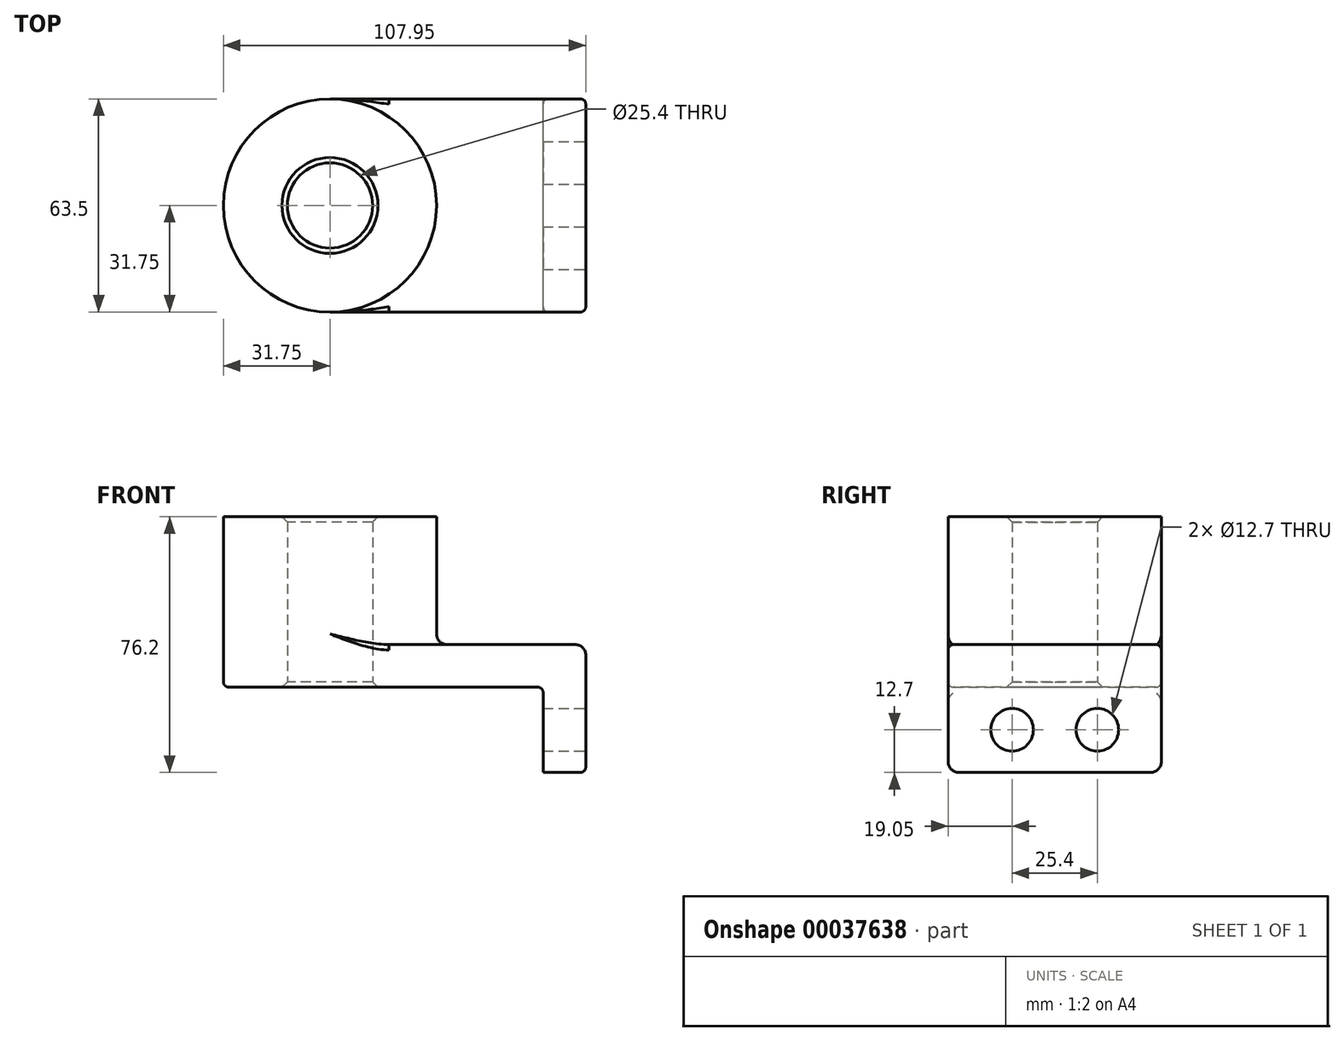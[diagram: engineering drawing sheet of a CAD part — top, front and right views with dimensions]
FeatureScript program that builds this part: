
annotation { "Feature Type Name" : "Feature", "Feature Type Description" : "" }
export const myFeature = defineFeature(function(context is Context, id is Id, definition is map)
    precondition{}
    {
        {
            var Q0;
            Q0=qCreatedBy(makeId("Top.planeOp"),FACE);
            var sketch = newSketch(context, id + "F0", { "sketchPlane" : qUnion([Q0])});
            skLineSegment(sketch, "E0.rect.bottom", {"start": v(38.1, -31.75) * mm, "end": v(-38.1, -31.75) * mm});
            skLineSegment(sketch, "E0.rect.top", {"start": v(38.1, 31.75) * mm, "end": v(-38.1, 31.75) * mm});
            skLineSegment(sketch, "E0.rect.left", {"start": v(38.1, -31.75) * mm, "end": v(38.1, 31.75) * mm});
            skLineSegment(sketch, "E0.rect.right", {"start": v(-38.1, -31.75) * mm, "end": v(-38.1, 31.75) * mm});
            skPoint(sketch, "E0.rect.middle", {"position": v(0, 0) * mm});
            skCircle(sketch, "E1", {"center": v(-38.1, 0) * mm, "radius": 31.75 * mm});
            skCircle(sketch, "E2", {"center": v(-38.1, 0) * mm, "radius": 12.7 * mm});
            skSolve(sketch);
        }
        {
            var Q0;
            Q0 = qSketchRegion(id + "F0", true);
            extrude(context, id + "F1", {"entities" : qUnion([Q0]), "depth" : 12.7 * mm});
        }
        {
            var Q0;
            {var subQ0=sQuery(id+"F0.wireOp",EDGE,"E2");var subQ1=sQuery(id+"F0.wireOp",EDGE,"E0.rect.right");var subQ3=makeQuery(id+"F0.imprint","INTERSECT",VERTEX,{"disambiguationData":[OD(0.0)],"derivedFrom":[subQ1,subQ0]});Q0=makeQuery(id+"F0.imprint","IMPRINT",FACE,{"disambiguationData":[TD([[makeQuery(id+"F0.imprint","IMPRINT",EDGE,{"disambiguationData":[TD([[subQ3,-1.0]])],"derivedFrom":subQ0}),-1.0]])]});}
            var Q1;
            {var subQ0=sQuery(id+"F0.wireOp",EDGE,"E2");var subQ1=sQuery(id+"F0.wireOp",EDGE,"E0.rect.right");var subQ3=makeQuery(id+"F0.imprint","INTERSECT",VERTEX,{"disambiguationData":[OD(0.0)],"derivedFrom":[subQ1,subQ0]});Q1=makeQuery(id+"F0.imprint","IMPRINT",FACE,{"disambiguationData":[TD([[makeQuery(id+"F0.imprint","IMPRINT",EDGE,{"disambiguationData":[TD([[subQ3,1.0]])],"derivedFrom":subQ0}),-1.0]])]});}
            var Q2;
            Q2=sQuery(id+"F0.wireOp",EDGE,"E1");
            var Q3;
            Q3=sQuery(id+"F0.wireOp",EDGE,"E2");
            extrude(context, id + "F2", {"entities" : qUnion([Q0, Q1]), "operationType" : NewBodyOperationType.ADD, "surfaceEntities" : qUnion([Q2, Q3]), "depth" : 50.8 * mm});
        }
        {
            var Q0;
            Q0=makeQuery(id+"F1.opExtrude","SWEPT_FACE",FACE,{"disambiguationData":[OSD([sQuery(id+"F0.wireOp",EDGE,"E0.rect.left")])]});
            var sketch = newSketch(context, id + "F3", { "sketchPlane" : qUnion([Q0])});
            skLineSegment(sketch, "E3.bottom", {"start": v(-31.75, 12.7) * mm, "end": v(31.75, 12.7) * mm});
            skLineSegment(sketch, "E3.top", {"start": v(-31.75, -25.4) * mm, "end": v(31.75, -25.4) * mm});
            skLineSegment(sketch, "E3.left", {"start": v(-31.75, 12.7) * mm, "end": v(-31.75, -25.4) * mm});
            skLineSegment(sketch, "E3.right", {"start": v(31.75, 12.7) * mm, "end": v(31.75, -25.4) * mm});
            skCircle(sketch, "E4", {"center": v(-12.7, -12.7) * mm, "radius": 6.35 * mm});
            skLineSegment(sketch, "E5", {"start": v(0, 0) * mm, "end": v(0, -25.4) * mm, "construction": true});
            skCircle(sketch, "E6.MirrorC", {"center": v(12.7, -12.7) * mm, "radius": 6.35 * mm});
            skSolve(sketch);
        }
        {
            var Q0;
            Q0 = qSketchRegion(id + "F3", true);
            extrude(context, id + "F4", {"entities" : qUnion([Q0]), "operationType" : NewBodyOperationType.ADD, "oppositeDirection" : true, "depth" : 12.7 * mm});
        }
        {
            var Q0;
            {var subQ0=sQuery(id+"F0.wireOp",EDGE,"E1");Q0=makeQuery(id+"F2.boolean.opBoolean","INTERSECT",EDGE,{"derivedFrom":[makeQuery(id+"F1.opExtrude","CAP_FACE",FACE,{"disambiguationData":[OSD([sQuery(id+"F0.wireOp",EDGE,"E0.rect.bottom"),sQuery(id+"F0.wireOp",EDGE,"E0.rect.top"),sQuery(id+"F0.wireOp",EDGE,"E0.rect.left"),subQ0,sQuery(id+"F0.wireOp",EDGE,"E2")])],"isStart":false}),makeQuery(id+"F2.opExtrude","SWEPT_FACE",FACE,{"disambiguationData":[OSD([subQ0])]})]});}
            var Q1;
            Q1=makeQuery(id+"F1.opExtrude","CAP_EDGE",EDGE,{"disambiguationData":[OSD([sQuery(id+"F0.wireOp",EDGE,"E0.rect.left")])],"isStart":false});
            var Q2;
            Q2=makeQuery(id+"F4.opExtrude","SWEPT_EDGE",EDGE,{"disambiguationData":[OSD([sQuery(id+"F3.wireOp",EDGE,"E3.top"),sQuery(id+"F3.wireOp",EDGE,"E3.left")])]});
            var Q3;
            Q3=makeQuery(id+"F4.opExtrude","SWEPT_EDGE",EDGE,{"disambiguationData":[OSD([sQuery(id+"F3.wireOp",EDGE,"E3.top"),sQuery(id+"F3.wireOp",EDGE,"E3.right")])]});
            fillet(context, id + "F5", {"entities" : qUnion([Q0, Q1, Q2, Q3]), "radius" : 3.17 * mm, "tangentPropagation" : true, "allowEdgeOverflow" : false});
        }
        {
            var Q0;
            Q0=makeQuery(id+"F1.opExtrude","CAP_EDGE",EDGE,{"disambiguationData":[OSD([sQuery(id+"F0.wireOp",EDGE,"E0.rect.bottom")])],"isStart":false});
            var Q1;
            Q1=makeQuery(id+"F1.opExtrude","CAP_EDGE",EDGE,{"disambiguationData":[OSD([sQuery(id+"F0.wireOp",EDGE,"E0.rect.bottom")])],"isStart":true});
            var Q2;
            Q2=makeQuery(id+"F4.boolean.opBoolean","INTERSECT",EDGE,{"derivedFrom":[makeQuery(id+"F1.opExtrude","CAP_FACE",FACE,{"disambiguationData":[OSD([sQuery(id+"F0.wireOp",EDGE,"E0.rect.bottom"),sQuery(id+"F0.wireOp",EDGE,"E0.rect.top"),sQuery(id+"F0.wireOp",EDGE,"E0.rect.left"),sQuery(id+"F0.wireOp",EDGE,"E1"),sQuery(id+"F0.wireOp",EDGE,"E2")])],"isStart":true}),makeQuery(id+"F4.opExtrude","CAP_FACE",FACE,{"disambiguationData":[OSD([sQuery(id+"F3.wireOp",EDGE,"E3.bottom"),sQuery(id+"F3.wireOp",EDGE,"E3.top"),sQuery(id+"F3.wireOp",EDGE,"E3.left"),sQuery(id+"F3.wireOp",EDGE,"E3.right"),sQuery(id+"F3.wireOp",EDGE,"E4"),sQuery(id+"F3.wireOp",EDGE,"E6.MirrorC")])],"isStart":false})]});
            fillet(context, id + "F6", {"entities" : qUnion([Q0, Q1, Q2]), "radius" : 1.59 * mm, "tangentPropagation" : true, "allowEdgeOverflow" : false});
        }
        {
            var Q0;
            {var subQ0=sQuery(id+"F0.wireOp",EDGE,"E2");Q0=makeQuery(id+"F2.boolean.opBoolean","MERGE",FACE,{"derivedFrom":[makeQuery(id+"F1.opExtrude","SWEPT_FACE",FACE,{"disambiguationData":[OSD([subQ0])]}),makeQuery(id+"F2.opExtrude","SWEPT_FACE",FACE,{"disambiguationData":[OSD([subQ0])]})]});}
            chamfer(context, id + "F7", {"entities" : qUnion([Q0]), "width" : 1.59 * mm, "tangentPropagation" : true});
        }
    });
